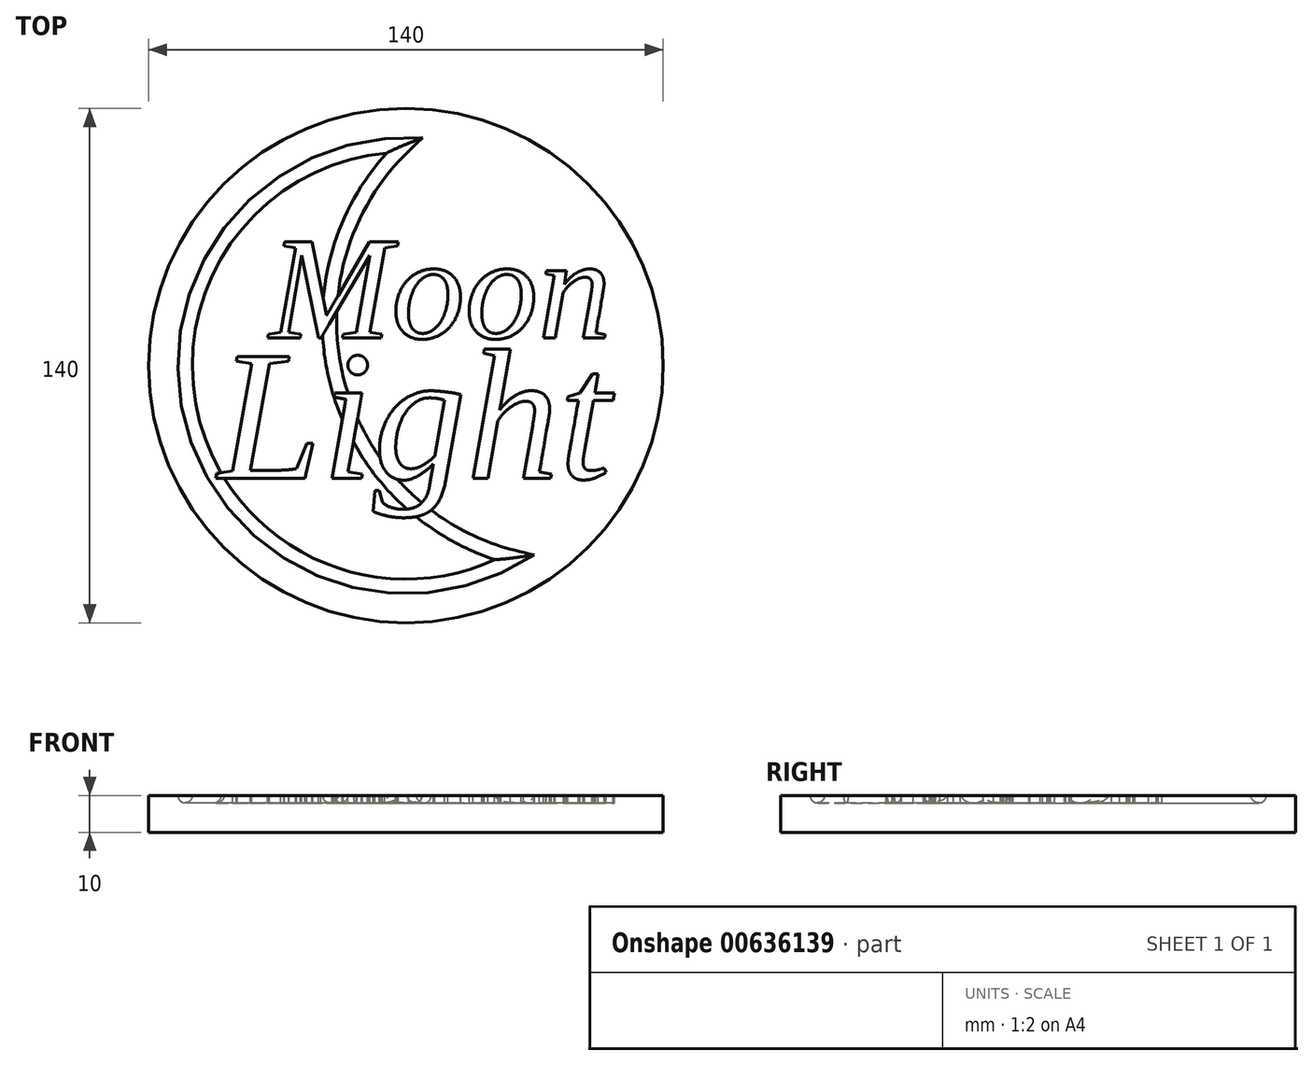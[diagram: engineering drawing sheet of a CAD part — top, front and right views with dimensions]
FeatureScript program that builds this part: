
annotation { "Feature Type Name" : "Feature", "Feature Type Description" : "" }
export const myFeature = defineFeature(function(context is Context, id is Id, definition is map)
    precondition{}
    {
        {
            var Q0;
            Q0=qCreatedBy(makeId("Top.planeOp"),FACE);
            var sketch = newSketch(context, id + "F0", { "sketchPlane" : qUnion([Q0])});
            skCircle(sketch, "E0", {"center": v(0, 0) * mm, "radius": 70 * mm});
            skSolve(sketch);
        }
        {
            var Q0;
            Q0=makeQuery(id+"F0.imprint","IMPRINT",FACE,{"disambiguationData":[TD([[makeQuery(id+"F0.imprint","IMPRINT",EDGE,{"derivedFrom":sQuery(id+"F0.wireOp",EDGE,"E0")}),1.0]])]});
            extrude(context, id + "F1", {"entities" : qUnion([Q0]), "oppositeDirection" : true, "depth" : 10 * mm, "offsetDistance" : 25 * mm});
        }
        {
            var Q0;
            Q0=makeQuery(id+"F1.opExtrude","CAP_FACE",FACE,{"disambiguationData":[OSD([sQuery(id+"F0.wireOp",EDGE,"E0")])],"isStart":true});
            var sketch = newSketch(context, id + "F2", { "sketchPlane" : qUnion([Q0])});
            skArc(sketch, "E1", {"start": v(0, 60.25) * mm, "mid": v(-58.2, -15.55) * mm, "end": v(30.05, -52.22) * mm});
            skArc(sketch, "E2", {"start": v(0, 60.25) * mm, "mid": v(-18.4, -4.92) * mm, "end": v(30.05, -52.22) * mm});
            skSolve(sketch);
        }
        {
            var Q0;
            Q0=qCreatedBy(makeId("Front.planeOp"),FACE);
            var sketch = newSketch(context, id + "F3", { "sketchPlane" : qUnion([Q0])});
            skCircle(sketch, "E3", {"center": v(-19.7, 0) * mm, "radius": 2 * mm});
            skSolve(sketch);
        }
        {
            var Q0;
            Q0=makeQuery(id+"F3.imprint","IMPRINT",FACE,{"disambiguationData":[TD([[makeQuery(id+"F3.imprint","IMPRINT",EDGE,{"derivedFrom":sQuery(id+"F3.wireOp",EDGE,"E3")}),1.0]])]});
            var Q1;
            Q1=sQuery(id+"F2.wireOp",EDGE,"E2");
            var Q2;
            Q2=sQuery(id+"F2.wireOp",EDGE,"E1");
            sweep(context, id + "F4", {"operationType" : NewBodyOperationType.REMOVE, "profiles" : qUnion([Q0]), "path" : qUnion([Q1, Q2])});
        }
        {
            var Q0;
            {var subQ0=sQuery(id+"F0.wireOp",EDGE,"E0");var subQ1=sQuery(id+"F3.wireOp",EDGE,"E3");Q0=makeQuery(id+"F4.boolean.opBoolean","SPLIT",FACE,{"disambiguationData":[TD([makeQuery(id+"F1.opExtrude","SWEPT_FACE",FACE,{"disambiguationData":[OSD([subQ0])]}),makeQuery(id+"F4.opSweep","SWEPT_FACE",FACE,{"disambiguationData":[OSD([sQuery(id+"F2.wireOp",EDGE,"E1"),subQ1])]}),makeQuery(id+"F4.opSweep","SWEPT_FACE",FACE,{"disambiguationData":[OSD([sQuery(id+"F2.wireOp",EDGE,"E2"),subQ1])]})])],"derivedFrom":makeQuery(id+"F1.opExtrude","CAP_FACE",FACE,{"disambiguationData":[OSD([subQ0])],"isStart":true})});}
            var sketch = newSketch(context, id + "F5", { "sketchPlane" : qUnion([Q0])});
            skText(sketch, "E4", { "text": "Moon", "fontName": "Tinos-Italic.ttf"});
            const initialGuessF5  = {"E4": [-0.03715, 0.00755, 1, 0, 0.02872]};
            skSetInitialGuess(sketch, initialGuessF5);
            skSolve(sketch);
        }
        {
            var Q0;
            {var subQ0=sQuery(id+"F5.wireOp",EDGE,"E4.sketch_text.stroke-14");Q0=makeQuery(id+"F5.imprint","IMPRINT",FACE,{"disambiguationData":[TD([[makeQuery(id+"F5.imprint","IMPRINT",EDGE,{"derivedFrom":subQ0}),1.0]])]});}
            var sketch = newSketch(context, id + "F6", { "sketchPlane" : qUnion([Q0])});
            skText(sketch, "E5", { "text": "Light", "fontName": "Tinos-Italic.ttf"});
            const initialGuessF6  = {"E5": [-0.05107, -0.03064, 1, 0, 0.03641]};
            skSetInitialGuess(sketch, initialGuessF6);
            skSolve(sketch);
        }
        {
            var Q0;
            Q0 = qSketchRegion(id + "F5", true);
            var Q1;
            Q1 = qSketchRegion(id + "F6", true);
            extrude(context, id + "F7", {"entities" : qUnion([Q0, Q1]), "operationType" : NewBodyOperationType.REMOVE, "oppositeDirection" : true, "depth" : 2 * mm, "offsetDistance" : 25 * mm});
        }
    });
